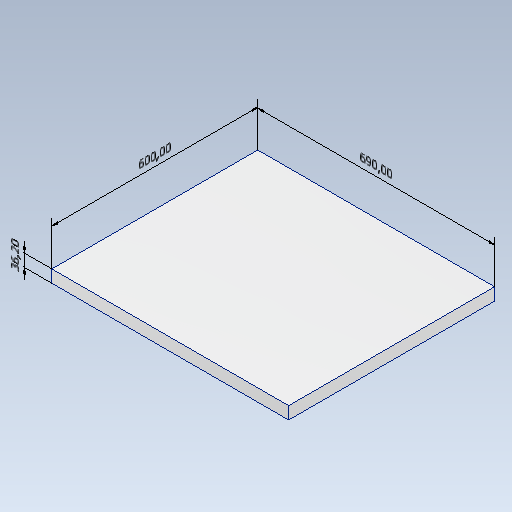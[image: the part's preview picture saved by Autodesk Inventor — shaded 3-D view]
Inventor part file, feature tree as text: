
AUTODESK INVENTOR PART (.ipt)
format: ipt  version: 2021 (Build 250183000, 183)  size: 113,664 bytes
history: native  units: mm
features: other x6, extrude x1, sketch x1
ambient origin geometry x8: Origin, YZ Plane, XZ Plane, XY Plane, X Axis, Y Axis, Z Axis, Center Point
bodies: Body1 (feature_tree)
feature tree (8):
  other  "piso2"
  other  "Sólido1"
  other  "Anotaciones"
  extrude  "Extrusión1"  Depth=600.0mm
  sketch  "Boceto1"  dims[d16=690.0mm d21=600.0mm d22=600.0mm d27=36.2mm d28=0.0mm d29=0.0mm d30=10.0mm d31=36.2mm d32=0.0mm d33=10.0mm d34=600.0mm d35=0.0mm d36=10.0mm d37=690.0mm]
  other  "Cota lineal 1"
  other  "Cota lineal 2"
  other  "Cota lineal 3"
